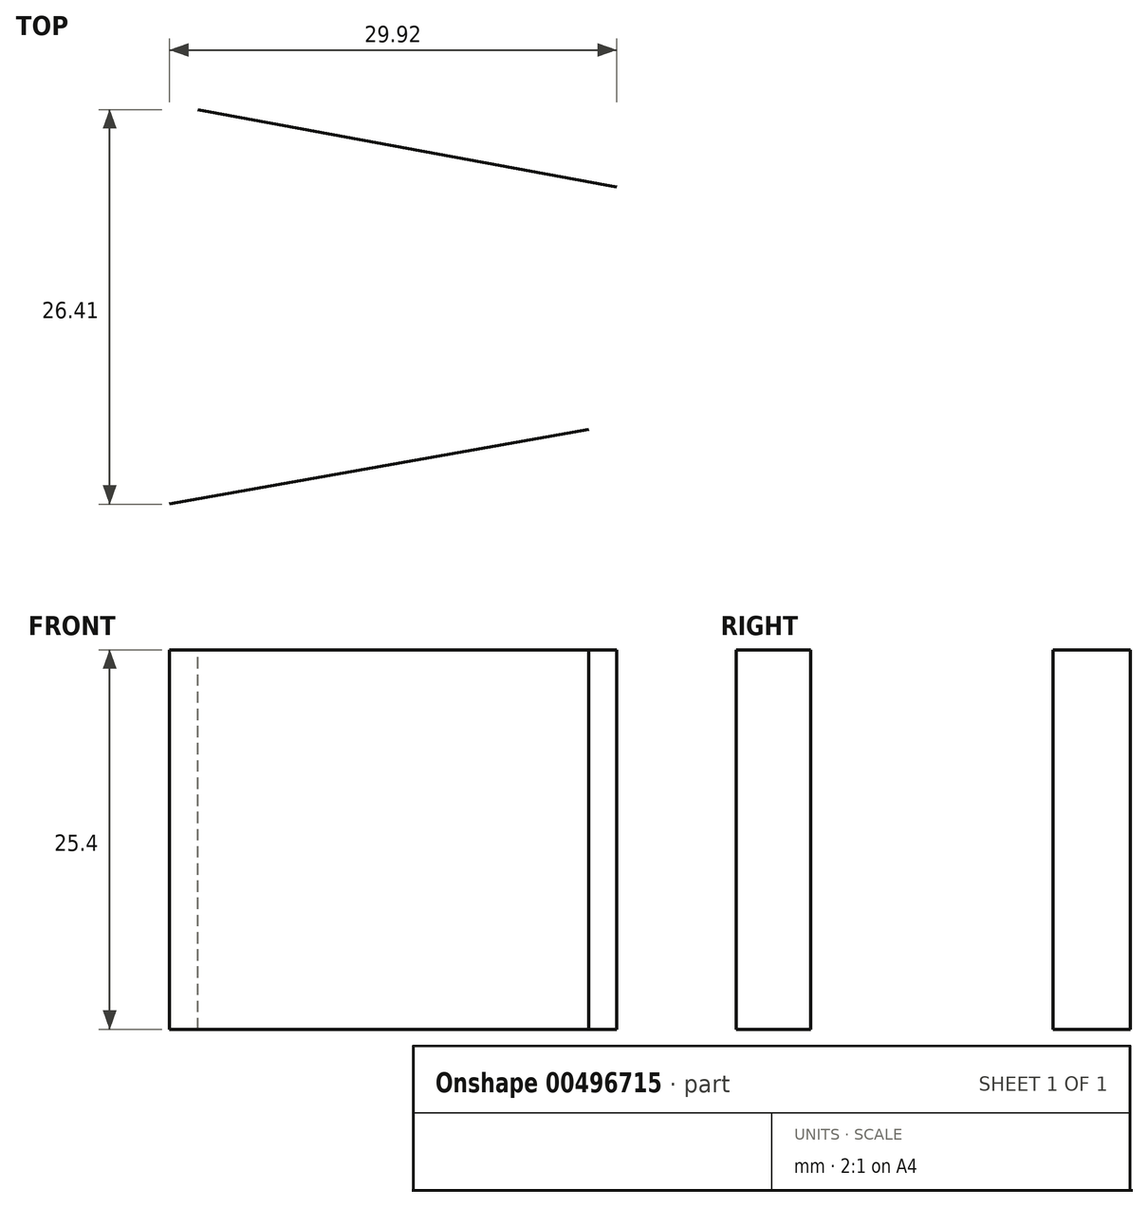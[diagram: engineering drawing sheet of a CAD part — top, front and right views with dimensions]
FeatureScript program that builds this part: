
annotation { "Feature Type Name" : "Feature", "Feature Type Description" : "" }
export const myFeature = defineFeature(function(context is Context, id is Id, definition is map)
    precondition{}
    {
        {
            var Q0;
            Q0=qCreatedBy(makeId("Top.planeOp"),FACE);
            var sketch = newSketch(context, id + "F0", { "sketchPlane" : qUnion([Q0])});
            skCircle(sketch, "E0", {"center": v(50.82, 0) * mm, "radius": 8.52 * mm});
            skLineSegment(sketch, "E1", {"start": v(52.3, -8.39) * mm, "end": v(24.24, -13.38) * mm});
            skLineSegment(sketch, "E2", {"start": v(54.16, 7.83) * mm, "end": v(26.13, 13.03) * mm});
            skCircle(sketch, "E3", {"center": v(21.86, 0) * mm, "radius": 13.59 * mm});
            skSolve(sketch);
        }
        {
            var Q0;
            Q0=sQuery(id+"F0.wireOp",EDGE,"E1");
            var Q1;
            Q1=sQuery(id+"F0.wireOp",EDGE,"E2");
            extrude(context, id + "F1", {"bodyType" : ToolBodyType.SURFACE, "surfaceEntities" : qUnion([Q0, Q1]), "depth" : 25.4 * mm, "offsetDistance" : 25.4 * mm});
        }
    });
